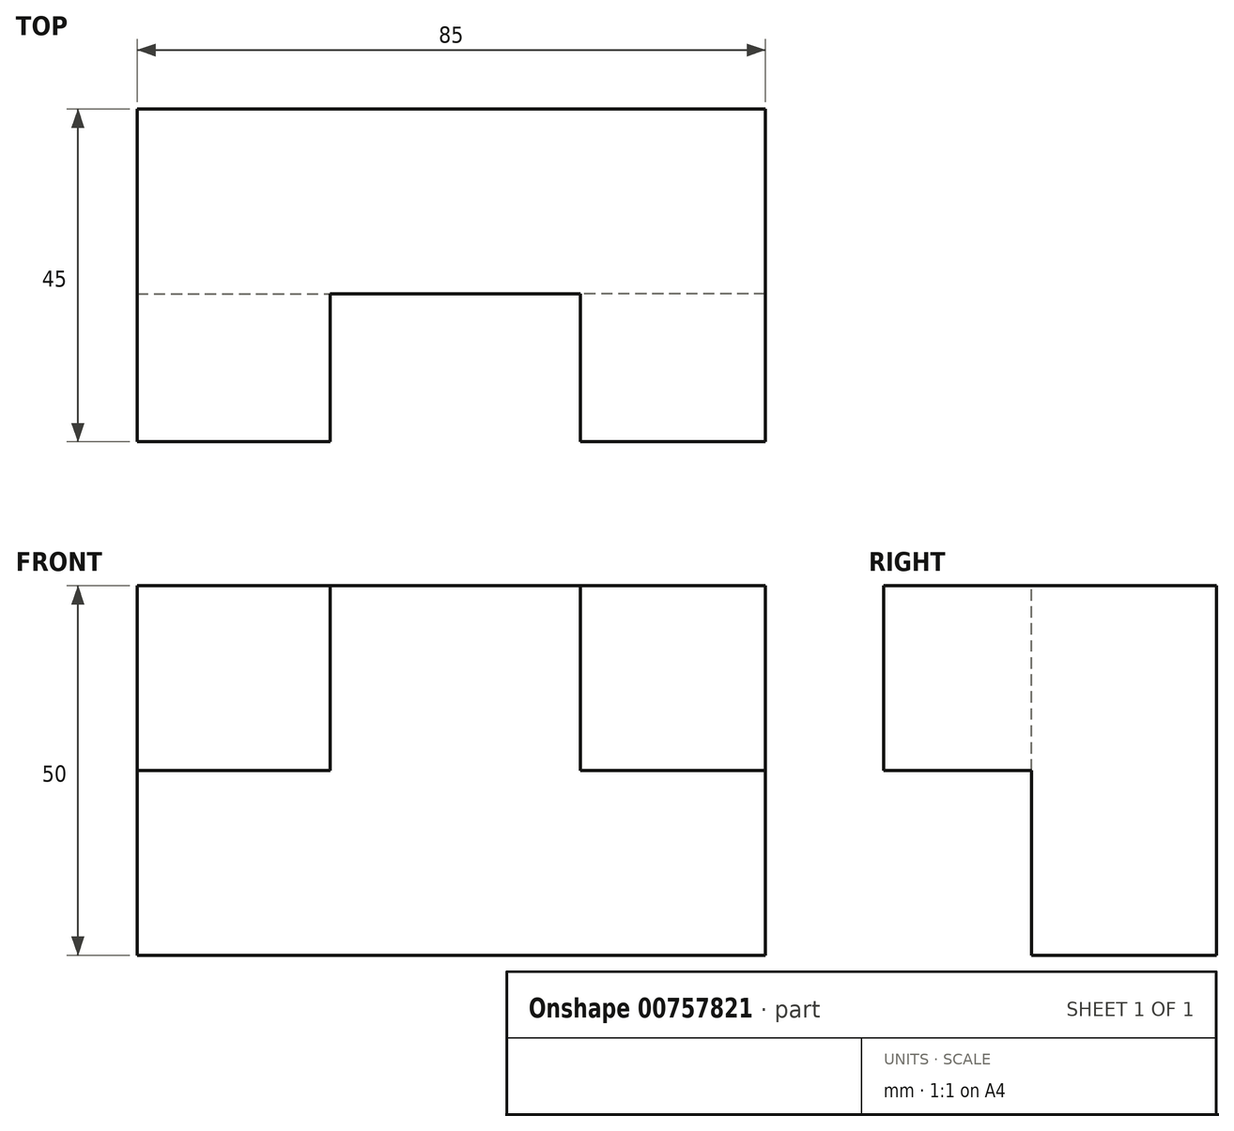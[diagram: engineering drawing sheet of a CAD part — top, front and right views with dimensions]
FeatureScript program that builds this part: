
annotation { "Feature Type Name" : "Feature", "Feature Type Description" : "" }
export const myFeature = defineFeature(function(context is Context, id is Id, definition is map)
    precondition{}
    {
        {
            var Q0;
            Q0=qCreatedBy(makeId("Front.planeOp"),FACE);
            var sketch = newSketch(context, id + "F0", { "sketchPlane" : qUnion([Q0])});
            skLineSegment(sketch, "E0.bottom", {"start": v(0, 0) * mm, "end": v(85, 0) * mm});
            skLineSegment(sketch, "E0.top", {"start": v(0, 50) * mm, "end": v(85, 50) * mm});
            skLineSegment(sketch, "E0.left", {"start": v(0, 0) * mm, "end": v(0, 50) * mm});
            skLineSegment(sketch, "E0.right", {"start": v(85, 0) * mm, "end": v(85, 50) * mm});
            skSolve(sketch);
        }
        {
            var Q0;
            Q0 = qSketchRegion(id + "F0", true);
            extrude(context, id + "F1", {"entities" : qUnion([Q0]), "depth" : 25 * mm, "offsetDistance" : 25 * mm});
        }
        {
            var Q0;
            Q0=makeQuery(id+"F1.opExtrude","CAP_FACE",FACE,{"disambiguationData":[OSD([sQuery(id+"F0.wireOp",EDGE,"E0.bottom"),sQuery(id+"F0.wireOp",EDGE,"E0.top"),sQuery(id+"F0.wireOp",EDGE,"E0.left"),sQuery(id+"F0.wireOp",EDGE,"E0.right")])],"isStart":false});
            var sketch = newSketch(context, id + "F2", { "sketchPlane" : qUnion([Q0])});
            skLineSegment(sketch, "E1.top", {"start": v(0, 50) * mm, "end": v(25, 50) * mm});
            skLineSegment(sketch, "E1.left", {"start": v(0, 27.67) * mm, "end": v(0, 50) * mm});
            skLineSegment(sketch, "E2.bottom", {"start": v(85, 25) * mm, "end": v(60, 25) * mm});
            skLineSegment(sketch, "E2.top", {"start": v(85, 50) * mm, "end": v(60, 50) * mm});
            skLineSegment(sketch, "E2.left", {"start": v(85, 25) * mm, "end": v(85, 50) * mm});
            skLineSegment(sketch, "E2.right", {"start": v(60, 25) * mm, "end": v(60, 50) * mm});
            skLineSegment(sketch, "E3.bottom", {"start": v(0, 25) * mm, "end": v(26.11, 25) * mm});
            skLineSegment(sketch, "E3.top", {"start": v(0, 50) * mm, "end": v(26.11, 50) * mm});
            skLineSegment(sketch, "E3.left", {"start": v(0, 25) * mm, "end": v(0, 50) * mm});
            skLineSegment(sketch, "E3.right", {"start": v(26.11, 25) * mm, "end": v(26.11, 50) * mm});
            skSolve(sketch);
        }
        {
            var Q0;
            Q0 = qSketchRegion(id + "F2", true);
            extrude(context, id + "F3", {"entities" : qUnion([Q0]), "operationType" : NewBodyOperationType.ADD, "depth" : 20 * mm, "offsetDistance" : 25 * mm});
        }
    });
